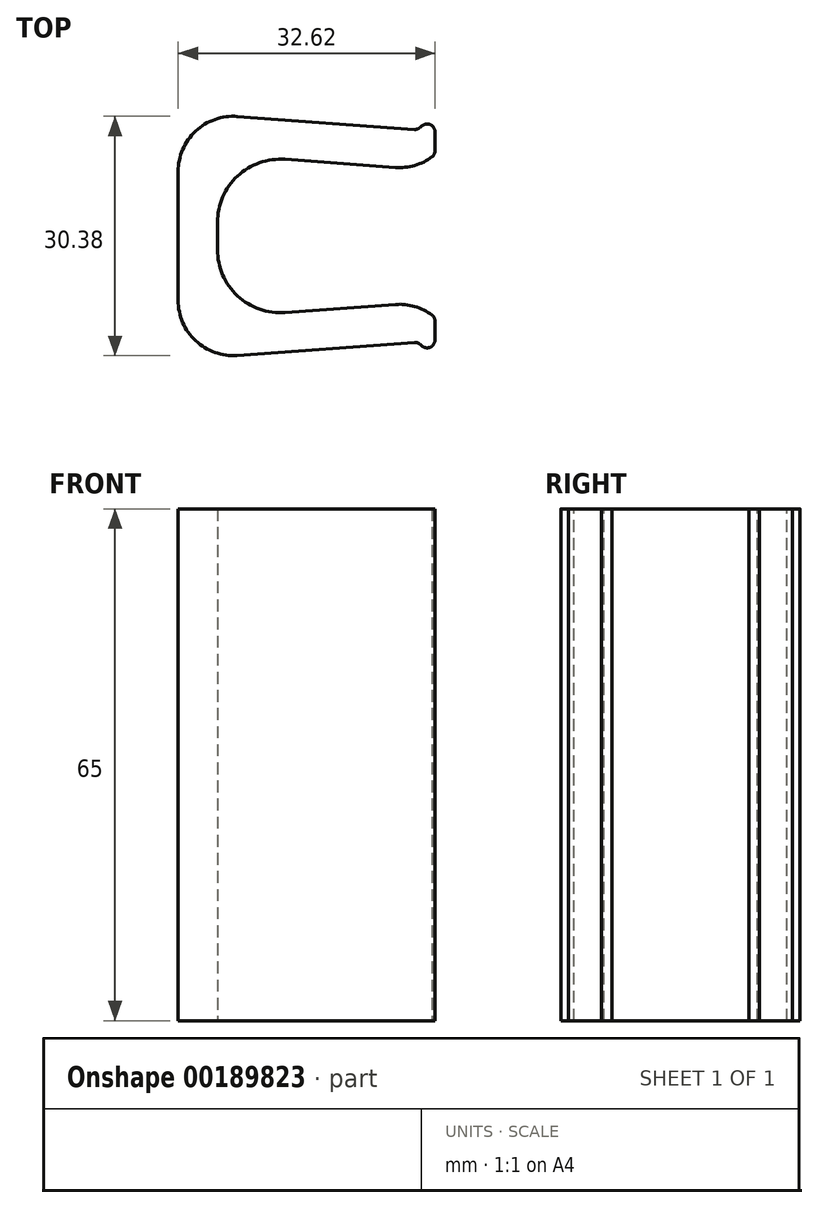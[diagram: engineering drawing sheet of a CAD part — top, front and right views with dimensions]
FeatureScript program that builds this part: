
annotation { "Feature Type Name" : "Feature", "Feature Type Description" : "" }
export const myFeature = defineFeature(function(context is Context, id is Id, definition is map)
    precondition{}
    {
        {
            var Q0;
            Q0=qCreatedBy(makeId("Top.planeOp"),FACE);
            var sketch = newSketch(context, id + "F0", { "sketchPlane" : qUnion([Q0])});
            skLineSegment(sketch, "E0.left", {"start": v(0, 0) * mm, "end": v(0, -10.36) * mm});
            skLineSegment(sketch, "E1", {"start": v(0, 0) * mm, "end": v(25.4, 0) * mm});
            skLineSegment(sketch, "E2", {"start": v(25.4, 0) * mm, "end": v(25.4, -8.5) * mm});
            skLineSegment(sketch, "E3", {"start": v(0, -10.36) * mm, "end": v(25.4, -8.5) * mm});
            skLineSegment(sketch, "E4.bottom", {"start": v(0, 0) * mm, "end": v(-5, 0) * mm});
            skLineSegment(sketch, "E4.top", {"start": v(0, -15.35) * mm, "end": v(-5, -15.35) * mm});
            skLineSegment(sketch, "E4.left", {"start": v(0, 0) * mm, "end": v(0, -15.35) * mm});
            skLineSegment(sketch, "E4.right", {"start": v(-5, 0) * mm, "end": v(-5, -15.35) * mm});
            skLineSegment(sketch, "E5", {"start": v(25.4, -8.5) * mm, "end": v(27.62, -10.36) * mm});
            skLineSegment(sketch, "E6", {"start": v(0, -15.36) * mm, "end": v(25.4, -13.5) * mm});
            skLineSegment(sketch, "E7", {"start": v(25.4, -13.5) * mm, "end": v(27.62, -15.36) * mm});
            skLineSegment(sketch, "E8", {"start": v(27.62, -10.36) * mm, "end": v(27.62, -15.36) * mm});
            skSolve(sketch);
        }
        {
            var Q0;
            {var subQ3=sQuery(id+"F0.wireOp",EDGE,"E4.bottom");Q0=makeQuery(id+"F0.imprint","IMPRINT",FACE,{"disambiguationData":[TD([[makeQuery(id+"F0.imprint","IMPRINT",EDGE,{"derivedFrom":subQ3}),1.0]])]});}
            var Q1;
            {var subQ1=sQuery(id+"F0.wireOp",EDGE,"E3");Q1=makeQuery(id+"F0.imprint","IMPRINT",FACE,{"disambiguationData":[TD([[makeQuery(id+"F0.imprint","IMPRINT",EDGE,{"derivedFrom":subQ1}),-1.0]])]});}
            extrude(context, id + "F1", {"entities" : qUnion([Q0, Q1]), "depth" : 65 * mm});
        }
        {
            var Q0;
            Q0=makeQuery(id+"F1.opExtrude","SWEPT_EDGE",EDGE,{"disambiguationData":[OSD([sQuery(id+"F0.wireOp",EDGE,"E7"),sQuery(id+"F0.wireOp",EDGE,"E8")])]});
            var Q1;
            Q1=makeQuery(id+"F1.opExtrude","SWEPT_EDGE",EDGE,{"disambiguationData":[OSD([sQuery(id+"F0.wireOp",EDGE,"E6"),sQuery(id+"F0.wireOp",EDGE,"E7")])]});
            var Q2;
            Q2=makeQuery(id+"F1.opExtrude","SWEPT_EDGE",EDGE,{"disambiguationData":[OSD([sQuery(id+"F0.wireOp",EDGE,"E5"),sQuery(id+"F0.wireOp",EDGE,"E8")])]});
            fillet(context, id + "F2", {"entities" : qUnion([Q0, Q1, Q2]), "radius" : 1 * mm, "tangentPropagation" : true, "allowEdgeOverflow" : false});
        }
        {
            var Q0;
            Q0=makeQuery(id+"F1.opExtrude","SWEPT_EDGE",EDGE,{"disambiguationData":[OSD([sQuery(id+"F0.wireOp",EDGE,"E2"),sQuery(id+"F0.wireOp",EDGE,"E3"),sQuery(id+"F0.wireOp",EDGE,"E5")])]});
            var Q1;
            Q1=makeQuery(id+"F1.opExtrude","SWEPT_EDGE",EDGE,{"disambiguationData":[OSD([sQuery(id+"F0.wireOp",EDGE,"E4.top"),sQuery(id+"F0.wireOp",EDGE,"E4.right")])]});
            fillet(context, id + "F3", {"entities" : qUnion([Q0, Q1]), "radius" : 7 * mm, "tangentPropagation" : true, "allowEdgeOverflow" : false});
        }
        {
            var Q0;
            Q0=makeQuery(id+"F1.opExtrude","SWEPT_EDGE",EDGE,{"disambiguationData":[OSD([sQuery(id+"F0.wireOp",EDGE,"E3"),sQuery(id+"F0.wireOp",EDGE,"E4.left")])]});
            fillet(context, id + "F4", {"entities" : qUnion([Q0]), "radius" : 8 * mm, "tangentPropagation" : true, "allowEdgeOverflow" : false});
        }
        {
            var Q0;
            Q0=makeQuery(id+"F1.opExtrude","SWEPT_BODY",BODY,{"disambiguationData":[OSD([sQuery(id+"F0.wireOp",EDGE,"E3"),sQuery(id+"F0.wireOp",EDGE,"E4.bottom"),sQuery(id+"F0.wireOp",EDGE,"E4.top"),sQuery(id+"F0.wireOp",EDGE,"E4.left"),sQuery(id+"F0.wireOp",EDGE,"E4.right"),sQuery(id+"F0.wireOp",EDGE,"E5"),sQuery(id+"F0.wireOp",EDGE,"E6"),sQuery(id+"F0.wireOp",EDGE,"E7"),sQuery(id+"F0.wireOp",EDGE,"E8")])]});
            var Q1;
            Q1=qCreatedBy(makeId("Front.planeOp"),FACE);
            mirror(context, id + "F5", {"operationType" : NewBodyOperationType.ADD, "entities" : qUnion([Q0]), "mirrorPlane" : qUnion([Q1])});
        }
    });
